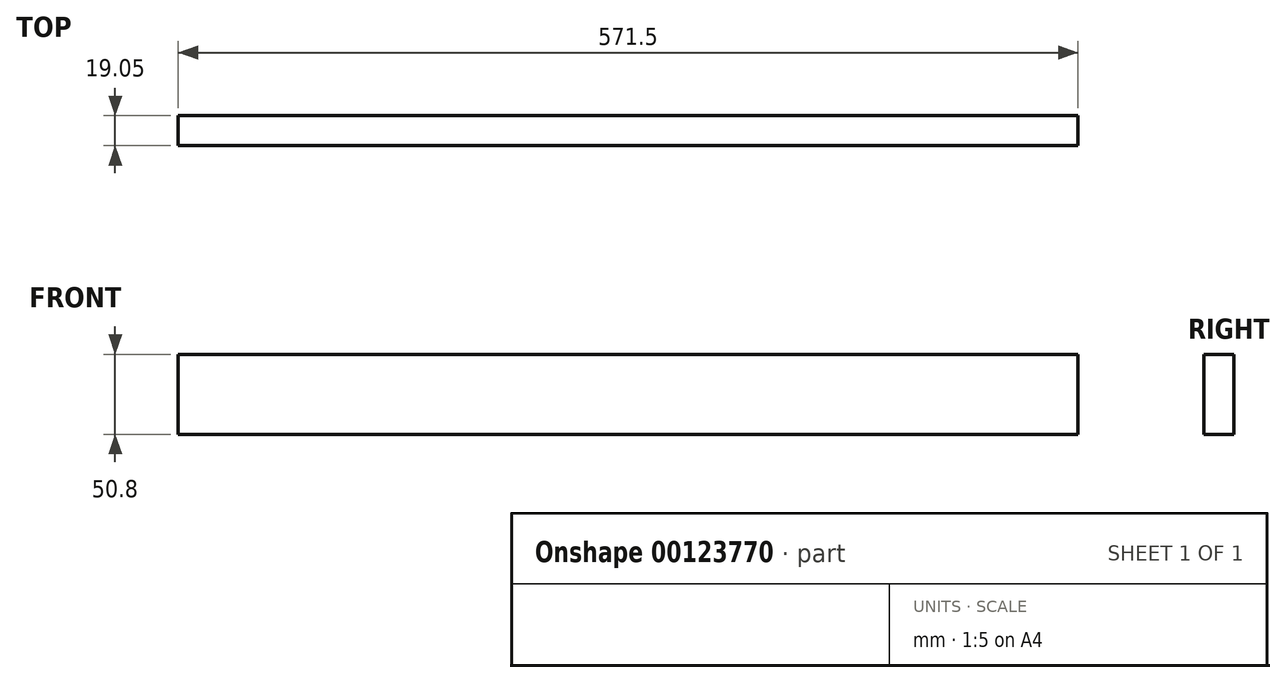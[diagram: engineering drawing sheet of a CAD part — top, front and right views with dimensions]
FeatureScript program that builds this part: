
annotation { "Feature Type Name" : "Feature", "Feature Type Description" : "" }
export const myFeature = defineFeature(function(context is Context, id is Id, definition is map)
    precondition{}
    {
        {
            var Q0;
            Q0=qCreatedBy(makeId("Front.planeOp"),FACE);
            var sketch = newSketch(context, id + "F0", { "sketchPlane" : qUnion([Q0])});
            skLineSegment(sketch, "E0.bottom", {"start": v(-282.82, -26.73) * mm, "end": v(288.68, -26.73) * mm});
            skLineSegment(sketch, "E0.top", {"start": v(-282.82, 24.07) * mm, "end": v(288.68, 24.07) * mm});
            skLineSegment(sketch, "E0.left", {"start": v(-282.82, -26.73) * mm, "end": v(-282.82, 24.07) * mm});
            skLineSegment(sketch, "E0.right", {"start": v(288.68, -26.73) * mm, "end": v(288.68, 24.07) * mm});
            skSolve(sketch);
        }
        {
            var Q0;
            Q0=makeQuery(id+"F0.imprint","IMPRINT",FACE,{"disambiguationData":[TD([[makeQuery(id+"F0.imprint","IMPRINT",EDGE,{"derivedFrom":sQuery(id+"F0.wireOp",EDGE,"E0.bottom")}),1.0]])]});
            extrude(context, id + "F1", {"entities" : qUnion([Q0]), "depth" : 19.05 * mm});
        }
    });
